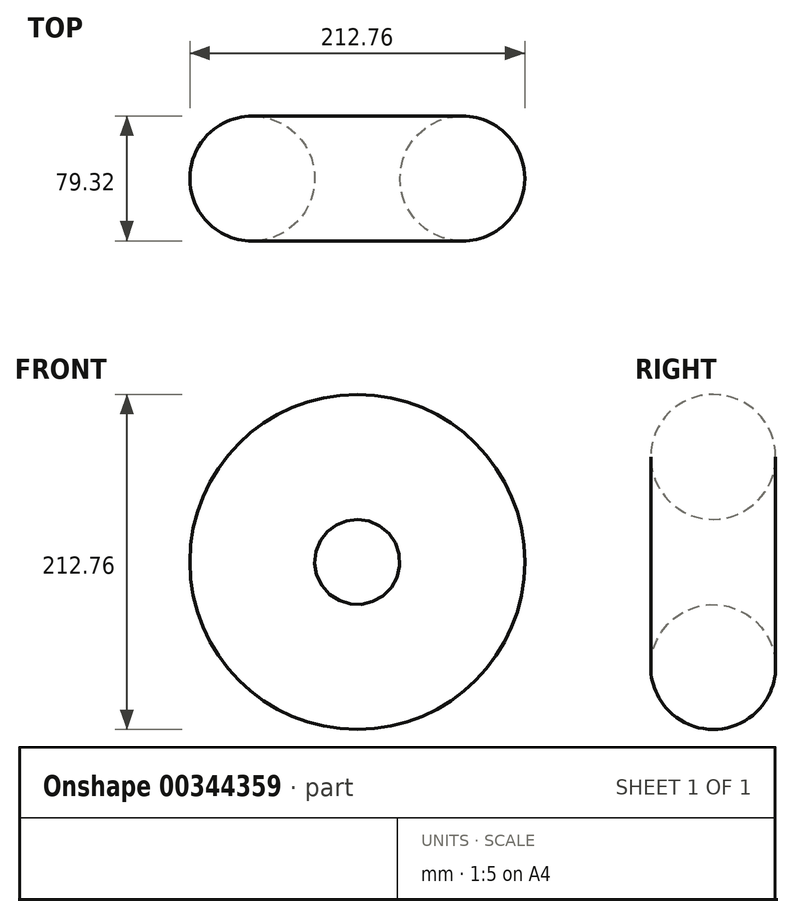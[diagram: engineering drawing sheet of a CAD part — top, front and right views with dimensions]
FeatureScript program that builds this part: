
annotation { "Feature Type Name" : "Feature", "Feature Type Description" : "" }
export const myFeature = defineFeature(function(context is Context, id is Id, definition is map)
    precondition{}
    {
        {
            var Q0;
            Q0=qCreatedBy(makeId("Top.planeOp"),FACE);
            var sketch = newSketch(context, id + "F0", { "sketchPlane" : qUnion([Q0])});
            skCircle(sketch, "E0", {"center": v(0, 0) * mm, "radius": 39.66 * mm});
            skSolve(sketch);
        }
        {
            var Q0;
            Q0=qCreatedBy(makeId("Top.planeOp"),FACE);
            var sketch = newSketch(context, id + "F1", { "sketchPlane" : qUnion([Q0])});
            skLineSegment(sketch, "E1", {"start": v(66.72, 36.66) * mm, "end": v(66.72, -42.53) * mm});
            skSolve(sketch);
        }
        {
            var Q0;
            Q0=makeQuery(id+"F0.imprint","IMPRINT",FACE,{"disambiguationData":[TD([[makeQuery(id+"F0.imprint","IMPRINT",EDGE,{"derivedFrom":sQuery(id+"F0.wireOp",EDGE,"E0")}),1.0]])]});
            var Q1;
            Q1=sQuery(id+"F1.wireOp",EDGE,"E1");
            revolve(context, id + "F2", {"entities" : qUnion([Q0]), "axis" : qUnion([Q1]), "revolveType" : RevolveType.FULL});
        }
    });
